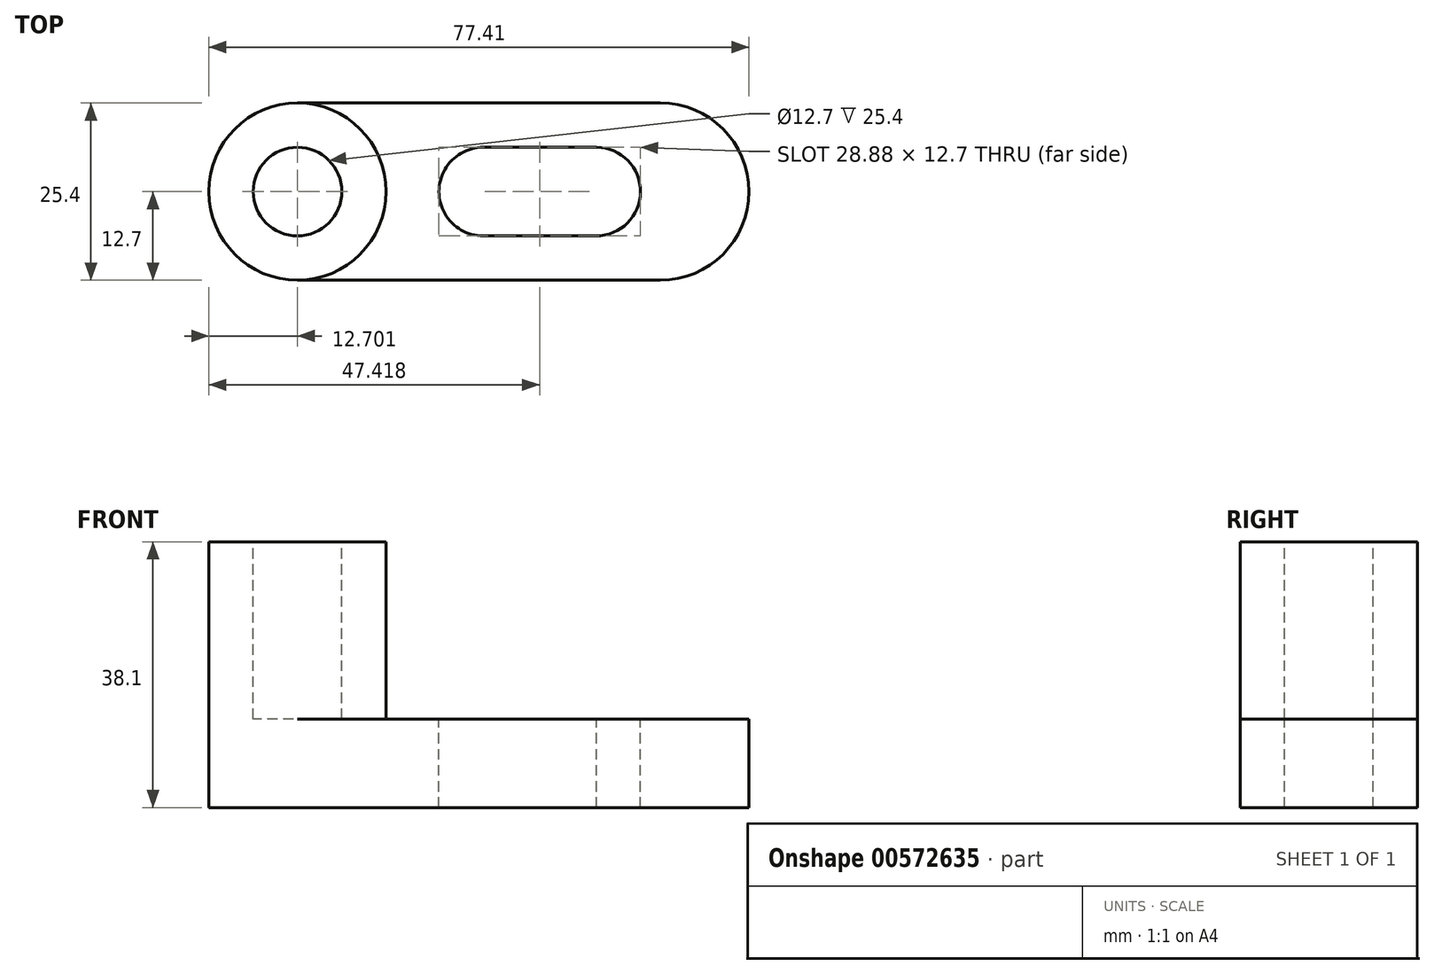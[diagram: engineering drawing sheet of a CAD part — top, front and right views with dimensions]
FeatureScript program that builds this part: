
annotation { "Feature Type Name" : "Feature", "Feature Type Description" : "" }
export const myFeature = defineFeature(function(context is Context, id is Id, definition is map)
    precondition{}
    {
        {
            var Q0;
            Q0=qCreatedBy(makeId("Front.planeOp"),FACE);
            var sketch = newSketch(context, id + "F0", { "sketchPlane" : qUnion([Q0])});
            skLineSegment(sketch, "E0", {"start": v(0, 0) * mm, "end": v(76.2, 0) * mm});
            skLineSegment(sketch, "E1", {"start": v(76.2, 0) * mm, "end": v(76.2, 12.7) * mm});
            skLineSegment(sketch, "E2", {"start": v(76.2, 12.7) * mm, "end": v(0, 12.7) * mm});
            skLineSegment(sketch, "E3", {"start": v(0, 12.7) * mm, "end": v(0, 0) * mm});
            skSolve(sketch);
        }
        {
            var Q0;
            Q0=makeQuery(id+"F0.imprint","IMPRINT",FACE,{"disambiguationData":[TD([[makeQuery(id+"F0.imprint","IMPRINT",EDGE,{"derivedFrom":sQuery(id+"F0.wireOp",EDGE,"E0")}),1.0]])]});
            extrude(context, id + "F1", {"entities" : qUnion([Q0]), "depth" : 25.4 * mm, "offsetDistance" : 25.4 * mm});
        }
        {
            var Q0;
            Q0=makeQuery(id+"F1.opExtrude","SWEPT_FACE",FACE,{"disambiguationData":[OSD([sQuery(id+"F0.wireOp",EDGE,"E2")])]});
            var sketch = newSketch(context, id + "F2", { "sketchPlane" : qUnion([Q0])});
            skCircle(sketch, "E4", {"center": v(11.5, -12.7) * mm, "radius": 12.7 * mm});
            skSolve(sketch);
        }
        {
            var Q0;
            {var subQ0=sQuery(id+"F2.wireOp",EDGE,"E4");var subQ1=sQuery(id+"F0.wireOp",EDGE,"E2");var subQ4=makeQuery(id+"F1.opExtrude","CAP_EDGE",EDGE,{"disambiguationData":[OSD([subQ1])],"isStart":true});var subQ5=makeQuery(id+"F2.imprint","INTERSECT",VERTEX,{"derivedFrom":[subQ4,subQ0]});Q0=makeQuery(id+"F2.imprint","IMPRINT",FACE,{"disambiguationData":[TD([[makeQuery(id+"F2.imprint","IMPRINT",EDGE,{"disambiguationData":[TD([[subQ5,-1.0]])],"derivedFrom":subQ0}),-1.0]])]});}
            var Q1;
            {var subQ0=sQuery(id+"F2.wireOp",EDGE,"E4");var subQ1=sQuery(id+"F0.wireOp",EDGE,"E2");var subQ4=makeQuery(id+"F1.opExtrude","CAP_EDGE",EDGE,{"disambiguationData":[OSD([subQ1])],"isStart":false});var subQ5=makeQuery(id+"F2.imprint","INTERSECT",VERTEX,{"derivedFrom":[subQ4,subQ0]});Q1=makeQuery(id+"F2.imprint","IMPRINT",FACE,{"disambiguationData":[TD([[makeQuery(id+"F2.imprint","IMPRINT",EDGE,{"disambiguationData":[TD([[subQ5,1.0]])],"derivedFrom":subQ0}),-1.0]])]});}
            extrude(context, id + "F3", {"entities" : qUnion([Q0, Q1]), "operationType" : NewBodyOperationType.REMOVE, "oppositeDirection" : true, "depth" : 12.7 * mm, "offsetDistance" : 25.4 * mm});
        }
        {
            var Q0;
            Q0=makeQuery(id+"F1.opExtrude","SWEPT_FACE",FACE,{"disambiguationData":[OSD([sQuery(id+"F0.wireOp",EDGE,"E2")])]});
            var sketch = newSketch(context, id + "F4", { "sketchPlane" : qUnion([Q0])});
            skCircle(sketch, "E5", {"center": v(11.5, -12.7) * mm, "radius": 12.7 * mm});
            skSolve(sketch);
        }
        {
            var Q0;
            {var subQ1=sQuery(id+"F0.wireOp",EDGE,"E2");var subQ2=makeQuery(id+"F1.opExtrude","SWEPT_EDGE",EDGE,{"disambiguationData":[OSD([subQ1,sQuery(id+"F0.wireOp",EDGE,"E3")])]});Q0=makeQuery(id+"F4.imprint","IMPRINT",FACE,{"disambiguationData":[TD([[makeQuery(id+"F4.imprint","IMPRINT",EDGE,{"derivedFrom":subQ2}),-1.0]])]});}
            extrude(context, id + "F5", {"entities" : qUnion([Q0]), "operationType" : NewBodyOperationType.ADD, "depth" : 25.4 * mm, "offsetDistance" : 25.4 * mm});
        }
        {
            var Q0;
            Q0=makeQuery(id+"F5.opExtrude","CAP_FACE",FACE,{"disambiguationData":[OSD([sQuery(id+"F0.wireOp",EDGE,"E2"),sQuery(id+"F0.wireOp",EDGE,"E3"),sQuery(id+"F4.wireOp",EDGE,"E5")])],"isStart":false});
            var sketch = newSketch(context, id + "F6", { "sketchPlane" : qUnion([Q0])});
            skCircle(sketch, "E6", {"center": v(11.5, -12.7) * mm, "radius": 6.35 * mm});
            skSolve(sketch);
        }
        {
            var Q0;
            Q0=makeQuery(id+"F6.imprint","IMPRINT",FACE,{"disambiguationData":[TD([[makeQuery(id+"F6.imprint","IMPRINT",EDGE,{"derivedFrom":sQuery(id+"F6.wireOp",EDGE,"E6")}),1.0]])]});
            extrude(context, id + "F7", {"entities" : qUnion([Q0]), "operationType" : NewBodyOperationType.REMOVE, "oppositeDirection" : true, "depth" : 25.4 * mm, "offsetDistance" : 25.4 * mm});
        }
        {
            var Q0;
            Q0=makeQuery(id+"F1.opExtrude","SWEPT_FACE",FACE,{"disambiguationData":[OSD([sQuery(id+"F0.wireOp",EDGE,"E2")])]});
            var sketch = newSketch(context, id + "F8", { "sketchPlane" : qUnion([Q0])});
            skCircle(sketch, "E7", {"center": v(38.12, -12.7) * mm, "radius": 6.35 * mm});
            skCircle(sketch, "E8", {"center": v(54.3, -12.7) * mm, "radius": 6.35 * mm});
            skLineSegment(sketch, "E9", {"start": v(54.37, -6.35) * mm, "end": v(38.12, -6.35) * mm});
            skLineSegment(sketch, "E10", {"start": v(38.12, -19.05) * mm, "end": v(54.3, -19.05) * mm});
            skArc(sketch, "E11", {"start": v(63.5, -25.4) * mm, "mid": v(76.2, -12.7) * mm, "end": v(63.5, 0) * mm});
            skLineSegment(sketch, "E12", {"start": v(63.5, 0) * mm, "end": v(76.2, 0) * mm});
            skLineSegment(sketch, "E13", {"start": v(63.5, -25.4) * mm, "end": v(76.2, -25.4) * mm});
            skSolve(sketch);
        }
        {
            var Q0;
            {var subQ0=sQuery(id+"F8.wireOp",EDGE,"E7");var subQ1=makeQuery(id+"F8.imprint","INTERSECT",VERTEX,{"derivedFrom":[subQ0,sQuery(id+"F8.wireOp",EDGE,"E9")]});Q0=makeQuery(id+"F8.imprint","IMPRINT",FACE,{"disambiguationData":[TD([[makeQuery(id+"F8.imprint","IMPRINT",EDGE,{"disambiguationData":[TD([[subQ1,-1.0]])],"derivedFrom":subQ0}),1.0]])]});}
            var Q1;
            {var subQ3=sQuery(id+"F8.wireOp",EDGE,"E10");Q1=makeQuery(id+"F8.imprint","IMPRINT",FACE,{"disambiguationData":[TD([[makeQuery(id+"F8.imprint","IMPRINT",EDGE,{"derivedFrom":subQ3}),1.0]])]});}
            var Q2;
            {var subQ0=sQuery(id+"F8.wireOp",EDGE,"E8");var subQ1=makeQuery(id+"F8.imprint","INTERSECT",VERTEX,{"derivedFrom":[subQ0,sQuery(id+"F8.wireOp",EDGE,"E10")]});Q2=makeQuery(id+"F8.imprint","IMPRINT",FACE,{"disambiguationData":[TD([[makeQuery(id+"F8.imprint","IMPRINT",EDGE,{"disambiguationData":[TD([[subQ1,1.0]])],"derivedFrom":subQ0}),1.0]])]});}
            var Q3;
            {var subQ0=sQuery(id+"F8.wireOp",EDGE,"E12");Q3=makeQuery(id+"F8.imprint","IMPRINT",FACE,{"disambiguationData":[TD([[makeQuery(id+"F8.imprint","IMPRINT",EDGE,{"derivedFrom":subQ0}),1.0]])]});}
            var Q4;
            {var subQ0=sQuery(id+"F8.wireOp",EDGE,"E13");Q4=makeQuery(id+"F8.imprint","IMPRINT",FACE,{"disambiguationData":[TD([[makeQuery(id+"F8.imprint","IMPRINT",EDGE,{"derivedFrom":subQ0}),-1.0]])]});}
            extrude(context, id + "F9", {"entities" : qUnion([Q0, Q1, Q2, Q3, Q4]), "operationType" : NewBodyOperationType.REMOVE, "oppositeDirection" : true, "depth" : 25.4 * mm, "offsetDistance" : 25.4 * mm});
        }
        {
            var Q0;
            Q0=makeQuery(id+"F5.opExtrude","CAP_FACE",FACE,{"disambiguationData":[OSD([sQuery(id+"F0.wireOp",EDGE,"E2"),sQuery(id+"F0.wireOp",EDGE,"E3"),sQuery(id+"F4.wireOp",EDGE,"E5")])],"isStart":false});
            var sketch = newSketch(context, id + "F10", { "sketchPlane" : qUnion([Q0])});
            skCircle(sketch, "E14", {"center": v(11.5, -12.7) * mm, "radius": 12.7 * mm});
            skSolve(sketch);
        }
        {
            var Q0;
            Q0 = qSketchRegion(id + "F10", true);
            extrude(context, id + "F11", {"entities" : qUnion([Q0]), "operationType" : NewBodyOperationType.ADD, "oppositeDirection" : true, "depth" : 38.1 * mm, "offsetDistance" : 25.4 * mm});
        }
        {
            var Q0;
            Q0=makeQuery(id+"F11.boolean.opBoolean","MERGE",FACE,{"derivedFrom":[makeQuery(id+"F5.opExtrude","CAP_FACE",FACE,{"disambiguationData":[OSD([sQuery(id+"F0.wireOp",EDGE,"E2"),sQuery(id+"F0.wireOp",EDGE,"E3"),sQuery(id+"F4.wireOp",EDGE,"E5")])],"isStart":false}),makeQuery(id+"F11.opExtrude","CAP_FACE",FACE,{"disambiguationData":[OSD([sQuery(id+"F10.wireOp",EDGE,"E14")])],"isStart":true})]});
            var sketch = newSketch(context, id + "F12", { "sketchPlane" : qUnion([Q0])});
            skCircle(sketch, "E15", {"center": v(11.5, -12.7) * mm, "radius": 6.35 * mm});
            skSolve(sketch);
        }
        {
            var Q0;
            Q0=makeQuery(id+"F12.imprint","IMPRINT",FACE,{"disambiguationData":[TD([[makeQuery(id+"F12.imprint","IMPRINT",EDGE,{"derivedFrom":sQuery(id+"F12.wireOp",EDGE,"E15")}),1.0]])]});
            extrude(context, id + "F13", {"entities" : qUnion([Q0]), "operationType" : NewBodyOperationType.REMOVE, "oppositeDirection" : true, "depth" : 25.4 * mm, "offsetDistance" : 25.4 * mm});
        }
    });
